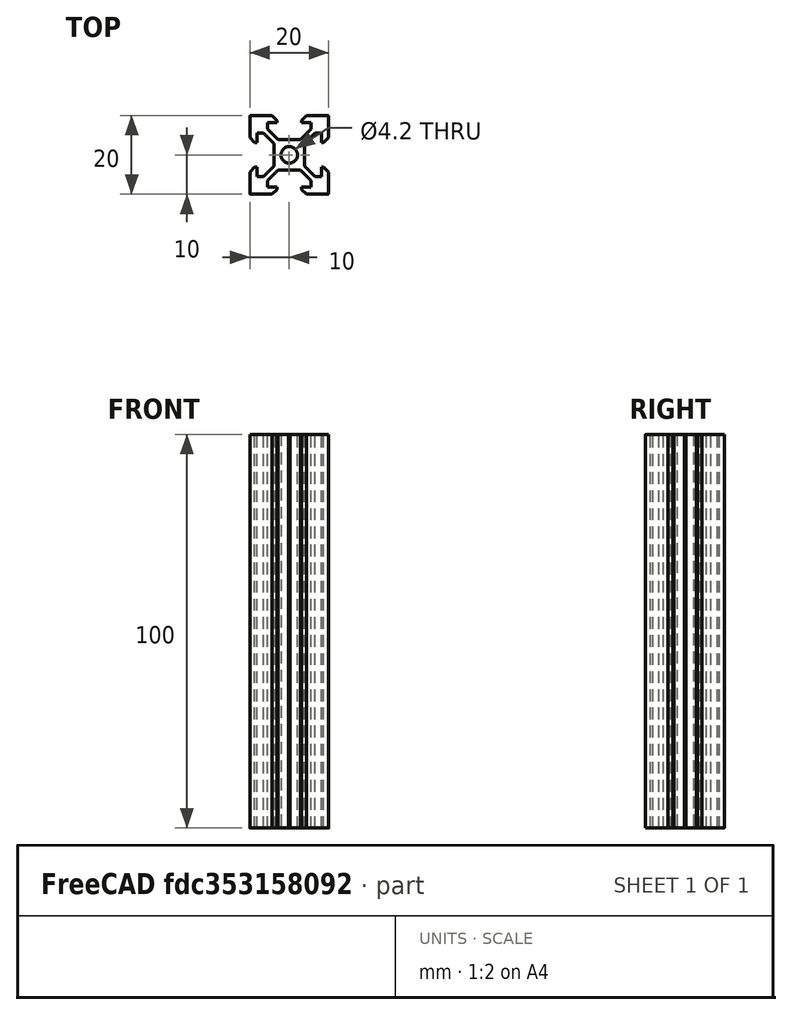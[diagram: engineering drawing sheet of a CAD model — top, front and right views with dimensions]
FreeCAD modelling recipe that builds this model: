
FCSTD DOCUMENT  (FreeCAD 0.19R23578 (Git))
Label: Vslot_2020
License: All rights reserved
LicenseURL: http://en.wikipedia.org/wiki/All_rights_reserved
objects: Sketcher::SketchObject×1, PartDesign::Pad×1, PartDesign::Chamfer×1, PartDesign::Fillet×1, PartDesign::Body×1, App::Part×1
note: 8 computed .brp shape members not serialized (recipe doc carries the construction recipe); baked Part::Feature solids carry a one-line shape summary decoded from their .brp

FEATURE [Sketcher::SketchObject] Sketch
  MapMode = 5
  Support = -> [XY_Plane001]
  sketch-geometry (57):
    g0: LineSegment StartX=0 StartY=3.72388 StartZ=0 EndX=0.176777 EndY=3.90066 EndZ=0
    g1: LineSegment StartX=0.176777 StartY=3.90066 StartZ=0 EndX=2.84 EndY=3.90066 EndZ=0
    g2: LineSegment StartX=2.84 StartY=3.90066 StartZ=0 EndX=5.49934 EndY=6.56 EndZ=0
    g3: LineSegment StartX=5.49934 StartY=6.56 StartZ=0 EndX=5.49934 EndY=8.2 EndZ=0
    g4: LineSegment StartX=5.49934 StartY=8.2 StartZ=0 EndX=3.1 EndY=8.2 EndZ=0
    g5: LineSegment StartX=3.1 StartY=8.2 StartZ=0 EndX=3.1 EndY=10 EndZ=0
    g6: LineSegment StartX=3.1 StartY=10 StartZ=0 EndX=10 EndY=10 EndZ=0
    g7: LineSegment StartX=10 StartY=10 StartZ=0 EndX=10 EndY=3.1 EndZ=0
    g8: LineSegment StartX=10 StartY=3.1 StartZ=0 EndX=8.2 EndY=3.1 EndZ=0
    g9: LineSegment StartX=8.2 StartY=3.1 StartZ=0 EndX=8.2 EndY=5.49934 EndZ=0
    g10: LineSegment StartX=8.2 StartY=5.49934 StartZ=0 EndX=6.56 EndY=5.49934 EndZ=0
    g11: LineSegment StartX=6.56 StartY=5.49934 StartZ=0 EndX=3.90066 EndY=2.84 EndZ=0
    g12: LineSegment StartX=3.90066 StartY=2.84 StartZ=0 EndX=3.90066 EndY=0.176777 EndZ=0
    g13: LineSegment StartX=3.90066 StartY=0.176777 StartZ=0 EndX=3.72388 EndY=0 EndZ=0
    g14: LineSegment StartX=0 StartY=3.72388 StartZ=0 EndX=-0.176777 EndY=3.90066 EndZ=0
    g15: LineSegment StartX=-0.176777 StartY=3.90066 StartZ=0 EndX=-2.84 EndY=3.90066 EndZ=0
    g16: LineSegment StartX=-2.84 StartY=3.90066 StartZ=0 EndX=-5.49934 EndY=6.56 EndZ=0
    g17: LineSegment StartX=-5.49934 StartY=6.56 StartZ=0 EndX=-5.49934 EndY=8.2 EndZ=0
    g18: LineSegment StartX=-5.49934 StartY=8.2 StartZ=0 EndX=-3.1 EndY=8.2 EndZ=0
    g19: LineSegment StartX=-3.1 StartY=8.2 StartZ=0 EndX=-3.1 EndY=10 EndZ=0
    g20: LineSegment StartX=-3.1 StartY=10 StartZ=0 EndX=-10 EndY=10 EndZ=0
    g21: LineSegment StartX=-10 StartY=10 StartZ=0 EndX=-10 EndY=3.1 EndZ=0
    g22: LineSegment StartX=-10 StartY=3.1 StartZ=0 EndX=-8.2 EndY=3.1 EndZ=0
    g23: LineSegment StartX=-8.2 StartY=3.1 StartZ=0 EndX=-8.2 EndY=5.49934 EndZ=0
    g24: LineSegment StartX=-8.2 StartY=5.49934 StartZ=0 EndX=-6.56 EndY=5.49934 EndZ=0
    g25: LineSegment StartX=-6.56 StartY=5.49934 StartZ=0 EndX=-3.90066 EndY=2.84 EndZ=0
    g26: LineSegment StartX=-3.90066 StartY=2.84 StartZ=0 EndX=-3.90066 EndY=0.176777 EndZ=0
    g27: LineSegment StartX=-3.90066 StartY=0.176777 StartZ=0 EndX=-3.72388 EndY=0 EndZ=0
    g28: LineSegment StartX=0 StartY=-3.72388 StartZ=0 EndX=0.176777 EndY=-3.90066 EndZ=0
    g29: LineSegment StartX=0.176777 StartY=-3.90066 StartZ=0 EndX=2.84 EndY=-3.90066 EndZ=0
    g30: LineSegment StartX=2.84 StartY=-3.90066 StartZ=0 EndX=5.49934 EndY=-6.56 EndZ=0
    g31: LineSegment StartX=5.49934 StartY=-6.56 StartZ=0 EndX=5.49934 EndY=-8.2 EndZ=0
    g32: LineSegment StartX=5.49934 StartY=-8.2 StartZ=0 EndX=3.1 EndY=-8.2 EndZ=0
    g33: LineSegment StartX=3.1 StartY=-8.2 StartZ=0 EndX=3.1 EndY=-10 EndZ=0
    g34: LineSegment StartX=3.1 StartY=-10 StartZ=0 EndX=10 EndY=-10 EndZ=0
    g35: LineSegment StartX=10 StartY=-10 StartZ=0 EndX=10 EndY=-3.1 EndZ=0
    g36: LineSegment StartX=10 StartY=-3.1 StartZ=0 EndX=8.2 EndY=-3.1 EndZ=0
    g37: LineSegment StartX=8.2 StartY=-3.1 StartZ=0 EndX=8.2 EndY=-5.49934 EndZ=0
    g38: LineSegment StartX=8.2 StartY=-5.49934 StartZ=0 EndX=6.56 EndY=-5.49934 EndZ=0
    g39: LineSegment StartX=6.56 StartY=-5.49934 StartZ=0 EndX=3.90066 EndY=-2.84 EndZ=0
    g40: LineSegment StartX=3.90066 StartY=-2.84 StartZ=0 EndX=3.90066 EndY=-0.176777 EndZ=0
    g41: LineSegment StartX=3.90066 StartY=-0.176777 StartZ=0 EndX=3.72388 EndY=0 EndZ=0
    g42: LineSegment StartX=0 StartY=-3.72388 StartZ=0 EndX=-0.176777 EndY=-3.90066 EndZ=0
    g43: LineSegment StartX=-0.176777 StartY=-3.90066 StartZ=0 EndX=-2.84 EndY=-3.90066 EndZ=0
    g44: LineSegment StartX=-2.84 StartY=-3.90066 StartZ=0 EndX=-5.49934 EndY=-6.56 EndZ=0
    g45: LineSegment StartX=-5.49934 StartY=-6.56 StartZ=0 EndX=-5.49934 EndY=-8.2 EndZ=0
    g46: LineSegment StartX=-5.49934 StartY=-8.2 StartZ=0 EndX=-3.1 EndY=-8.2 EndZ=0
    g47: LineSegment StartX=-3.1 StartY=-8.2 StartZ=0 EndX=-3.1 EndY=-10 EndZ=0
    g48: LineSegment StartX=-3.1 StartY=-10 StartZ=0 EndX=-10 EndY=-10 EndZ=0
    g49: LineSegment StartX=-10 StartY=-10 StartZ=0 EndX=-10 EndY=-3.1 EndZ=0
    g50: LineSegment StartX=-10 StartY=-3.1 StartZ=0 EndX=-8.2 EndY=-3.1 EndZ=0
    g51: LineSegment StartX=-8.2 StartY=-3.1 StartZ=0 EndX=-8.2 EndY=-5.49934 EndZ=0
    g52: LineSegment StartX=-8.2 StartY=-5.49934 StartZ=0 EndX=-6.56 EndY=-5.49934 EndZ=0
    g53: LineSegment StartX=-6.56 StartY=-5.49934 StartZ=0 EndX=-3.90066 EndY=-2.84 EndZ=0
    g54: LineSegment StartX=-3.90066 StartY=-2.84 StartZ=0 EndX=-3.90066 EndY=-0.176777 EndZ=0
    g55: LineSegment StartX=-3.90066 StartY=-0.176777 StartZ=0 EndX=-3.72388 EndY=0 EndZ=0
    g56: Circle CenterX=0 CenterY=0 CenterZ=0 NormalX=0 NormalY=0 NormalZ=1 AngleXU=0 Radius=2.1
FEATURE [PartDesign::Pad] Pad
  Direction = (1,1,1)
  Length = 100
  Length2 = 100
  Profile = -> Sketch
  Type = 0
FEATURE [PartDesign::Chamfer] Chamfer
  Angle = 45
  Base = -> Pad [Edge65,Edge101,Edge59,Edge149,Edge17,Edge107,Edge143,Edge23]
  BaseFeature = -> Pad
  ChamferType = 2
  FlipDirection = false
  Size = 1.25
  Size2 = 1
  SupportTransform = false
FEATURE [PartDesign::Fillet] Fillet
  Base = -> Chamfer [Edge190,Edge167,Edge135,Edge158]
  BaseFeature = -> Chamfer
  Radius = 0.2
  SupportTransform = false
FEATURE [PartDesign::Body] Body
  Group = -> [Sketch,Pad,Chamfer,Fillet]
  Origin = -> Origin001
  Tip = -> Fillet
FEATURE [App::Part] Part
  Group = -> [Body]
  Origin = -> Origin
